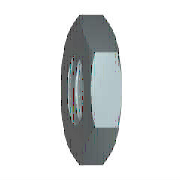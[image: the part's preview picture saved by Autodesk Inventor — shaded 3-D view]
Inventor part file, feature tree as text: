
AUTODESK INVENTOR PART (.ipt)
format: ipt  version: 2013 (Build 170138000, 138)  size: 171,008 bytes
history: native  units: mm (DEFAULTED — no unit token found)
features: sketch x3, chamfer x1, hole x1, other x1, plane x1
ambient origin geometry x7: Origin, YZ Plane, XZ Plane, X Axis, Y Axis, Z Axis, Center Point
bodies: Solid1 (feature_tree), Body (feature_tree)
feature tree (7):
  chamfer  "Chamfer1"  Angle=30.0deg  [1 undecoded]
  hole  "Thread"  [1 undecoded]
  other  "Work Axis1"
  plane  "Work Plane1"
  sketch  "Sketch1"  dims[d0=12.846274mm]
  sketch  "Sketch2"  dims[d1=4.0894mm]
  sketch  "Sketch3"  dims[d2=0.0mm d3=30.0deg d4=30.0deg d5=11.1252mm d6=11.1252mm d7=90.0deg d25=4.9784mm d26=6.0mm d27=4.0mm d28=2.0mm d29=14.3117mm d30=8.0mm d31=20.594885mm d8=0.687408mm d9=30.0deg d10=0.687408mm d11=30.0deg d13=0.0mm d14=0.0mm d39=0.0mm d40=0.687408mm d41=0.687408mm d42=0.0mm]
note: 2 required parameter values undecoded (feature->parameter linkage not recoverable at this tier; creation-order binding heuristic only, values carry confidence <= 0.55)
